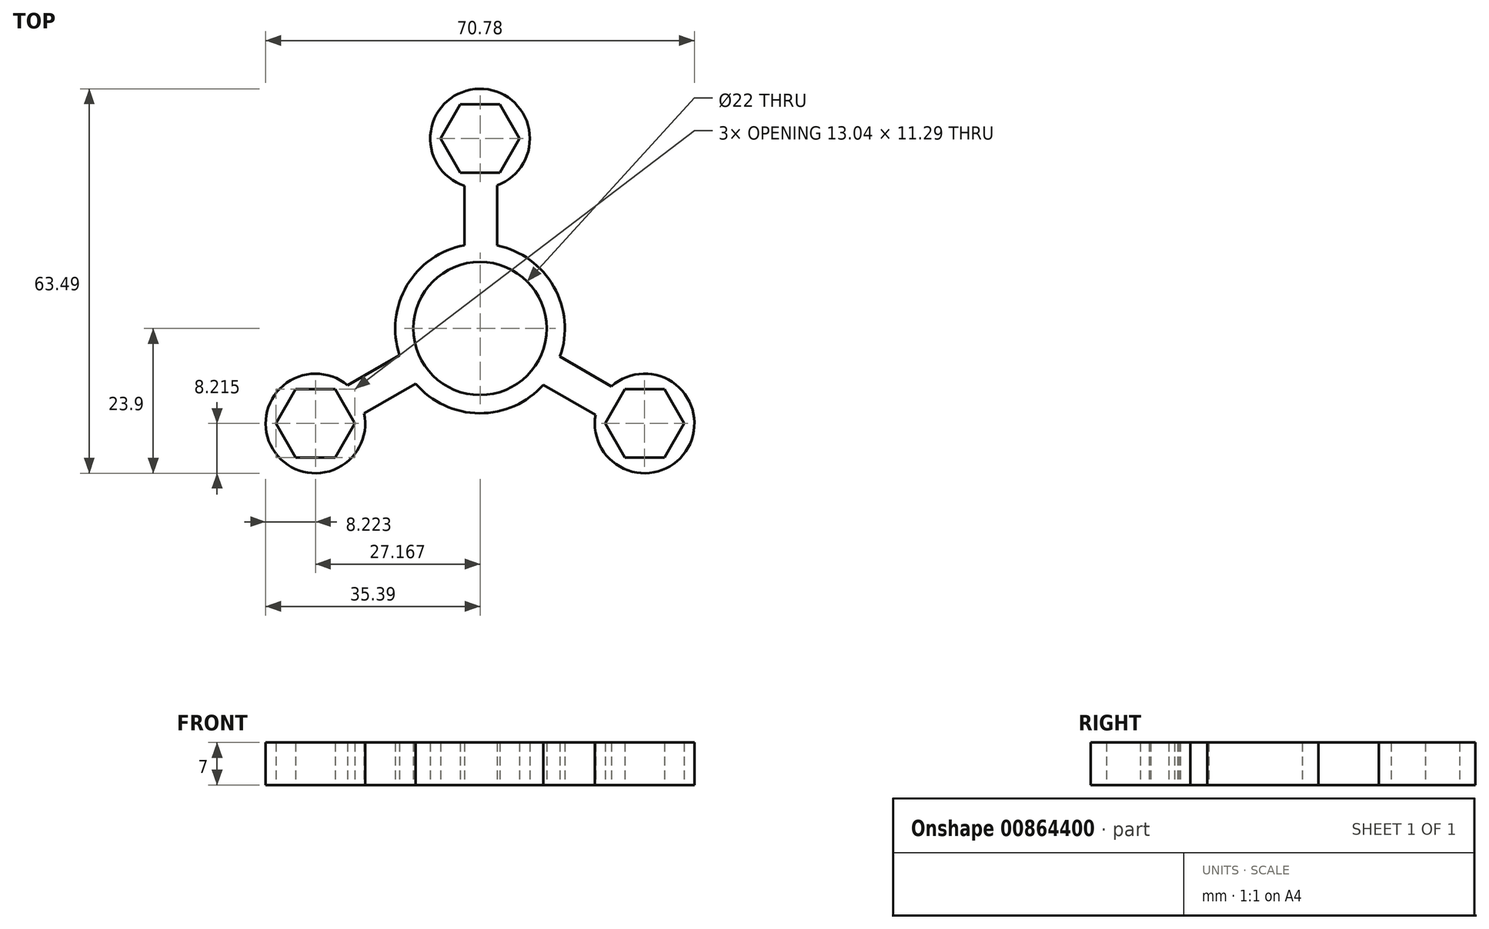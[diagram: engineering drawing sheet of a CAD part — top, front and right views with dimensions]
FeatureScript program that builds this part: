
annotation { "Feature Type Name" : "Feature", "Feature Type Description" : "" }
export const myFeature = defineFeature(function(context is Context, id is Id, definition is map)
    precondition{}
    {
        {
            var Q0;
            Q0=qCreatedBy(makeId("Top.planeOp"),FACE);
            var sketch = newSketch(context, id + "F0", { "sketchPlane" : qUnion([Q0])});
            skCircle(sketch, "E0", {"center": v(0, 0) * mm, "radius": 40 * mm, "construction": true});
            skCircle(sketch, "E1", {"center": v(0, 0) * mm, "radius": 11 * mm});
            skCircle(sketch, "E2.0", {"center": v(0, 0) * mm, "radius": 14 * mm});
            skCircle(sketch, "E3.cCircle", {"center": v(0, 31.37) * mm, "radius": 5.65 * mm, "construction": true});
            skLineSegment(sketch, "E3.0", {"start": v(3.26, 25.72) * mm, "end": v(-3.26, 25.72) * mm});
            skLineSegment(sketch, "E3.1", {"start": v(-3.26, 25.72) * mm, "end": v(-6.52, 31.37) * mm});
            skLineSegment(sketch, "E3.2", {"start": v(-6.52, 31.37) * mm, "end": v(-3.26, 37.02) * mm});
            skLineSegment(sketch, "E3.3", {"start": v(-3.26, 37.02) * mm, "end": v(3.26, 37.02) * mm});
            skLineSegment(sketch, "E3.4", {"start": v(3.26, 37.02) * mm, "end": v(6.52, 31.37) * mm});
            skLineSegment(sketch, "E3.5", {"start": v(6.52, 31.37) * mm, "end": v(3.26, 25.72) * mm});
            skPoint(sketch, "E3.0.midPoint", {"position": v(0, 25.72) * mm});
            skCircle(sketch, "E4", {"center": v(0, 31.37) * mm, "radius": 8.22 * mm});
            skLineSegment(sketch, "E5", {"start": v(-2.58, 23.57) * mm, "end": v(-2.58, 13.76) * mm});
            skLineSegment(sketch, "E6", {"start": v(2.81, 23.65) * mm, "end": v(2.81, 13.71) * mm});
            skCircle(sketch, "E7.1.0", {"center": v(-27.17, -15.68) * mm, "radius": 8.22 * mm});
            skLineSegment(sketch, "E7.1.1", {"start": v(-21.89, -9.39) * mm, "end": v(-13.28, -4.42) * mm});
            skLineSegment(sketch, "E7.1.2", {"start": v(-19.12, -14.01) * mm, "end": v(-10.63, -9.11) * mm});
            skLineSegment(sketch, "E7.1.3", {"start": v(-23.9, -10.04) * mm, "end": v(-20.65, -15.68) * mm});
            skLineSegment(sketch, "E7.1.4", {"start": v(-30.43, -10.04) * mm, "end": v(-23.9, -10.04) * mm});
            skLineSegment(sketch, "E7.1.5", {"start": v(-33.69, -15.68) * mm, "end": v(-30.43, -10.04) * mm});
            skLineSegment(sketch, "E7.1.6", {"start": v(-30.43, -21.33) * mm, "end": v(-33.69, -15.68) * mm});
            skLineSegment(sketch, "E7.1.7", {"start": v(-23.9, -21.33) * mm, "end": v(-30.43, -21.33) * mm});
            skLineSegment(sketch, "E7.1.8", {"start": v(-20.65, -15.68) * mm, "end": v(-23.9, -21.33) * mm});
            skCircle(sketch, "E7.2.0", {"center": v(27.17, -15.68) * mm, "radius": 8.22 * mm});
            skLineSegment(sketch, "E7.2.1", {"start": v(19.07, -14.26) * mm, "end": v(10.47, -9.3) * mm});
            skLineSegment(sketch, "E7.2.2", {"start": v(21.7, -9.55) * mm, "end": v(13.2, -4.65) * mm});
            skLineSegment(sketch, "E7.2.3", {"start": v(20.65, -15.68) * mm, "end": v(23.9, -10.04) * mm});
            skLineSegment(sketch, "E7.2.4", {"start": v(23.9, -21.33) * mm, "end": v(20.65, -15.68) * mm});
            skLineSegment(sketch, "E7.2.5", {"start": v(30.43, -21.33) * mm, "end": v(23.9, -21.33) * mm});
            skLineSegment(sketch, "E7.2.6", {"start": v(33.69, -15.68) * mm, "end": v(30.43, -21.33) * mm});
            skLineSegment(sketch, "E7.2.7", {"start": v(30.43, -10.04) * mm, "end": v(33.69, -15.68) * mm});
            skLineSegment(sketch, "E7.2.8", {"start": v(23.9, -10.04) * mm, "end": v(30.43, -10.04) * mm});
            skSolve(sketch);
        }
        {
            var Q0;
            Q0=makeQuery(id+"F0.imprint","IMPRINT",FACE,{"disambiguationData":[TD([[makeQuery(id+"F0.imprint","IMPRINT",EDGE,{"derivedFrom":sQuery(id+"F0.wireOp",EDGE,"E3.0")}),1.0]])]});
            var Q1;
            {var subQ0=sQuery(id+"F0.wireOp",EDGE,"E5");Q1=makeQuery(id+"F0.imprint","IMPRINT",FACE,{"disambiguationData":[TD([[makeQuery(id+"F0.imprint","IMPRINT",EDGE,{"derivedFrom":subQ0}),1.0]])]});}
            var Q2;
            Q2=makeQuery(id+"F0.imprint","IMPRINT",FACE,{"disambiguationData":[TD([[makeQuery(id+"F0.imprint","IMPRINT",EDGE,{"derivedFrom":sQuery(id+"F0.wireOp",EDGE,"E1")}),-1.0]])]});
            var Q3;
            {var subQ0=sQuery(id+"F0.wireOp",EDGE,"E7.1.1");Q3=makeQuery(id+"F0.imprint","IMPRINT",FACE,{"disambiguationData":[TD([[makeQuery(id+"F0.imprint","IMPRINT",EDGE,{"derivedFrom":subQ0}),-1.0]])]});}
            var Q4;
            Q4=makeQuery(id+"F0.imprint","IMPRINT",FACE,{"disambiguationData":[TD([[makeQuery(id+"F0.imprint","IMPRINT",EDGE,{"derivedFrom":sQuery(id+"F0.wireOp",EDGE,"E7.1.3")}),1.0]])]});
            var Q5;
            {var subQ0=sQuery(id+"F0.wireOp",EDGE,"E7.2.1");Q5=makeQuery(id+"F0.imprint","IMPRINT",FACE,{"disambiguationData":[TD([[makeQuery(id+"F0.imprint","IMPRINT",EDGE,{"derivedFrom":subQ0}),-1.0]])]});}
            var Q6;
            Q6=makeQuery(id+"F0.imprint","IMPRINT",FACE,{"disambiguationData":[TD([[makeQuery(id+"F0.imprint","IMPRINT",EDGE,{"derivedFrom":sQuery(id+"F0.wireOp",EDGE,"E7.2.3")}),1.0]])]});
            extrude(context, id + "F1", {"entities" : qUnion([Q0, Q1, Q2, Q3, Q4, Q5, Q6]), "depth" : 7 * mm, "offsetDistance" : 25 * mm});
        }
    });
